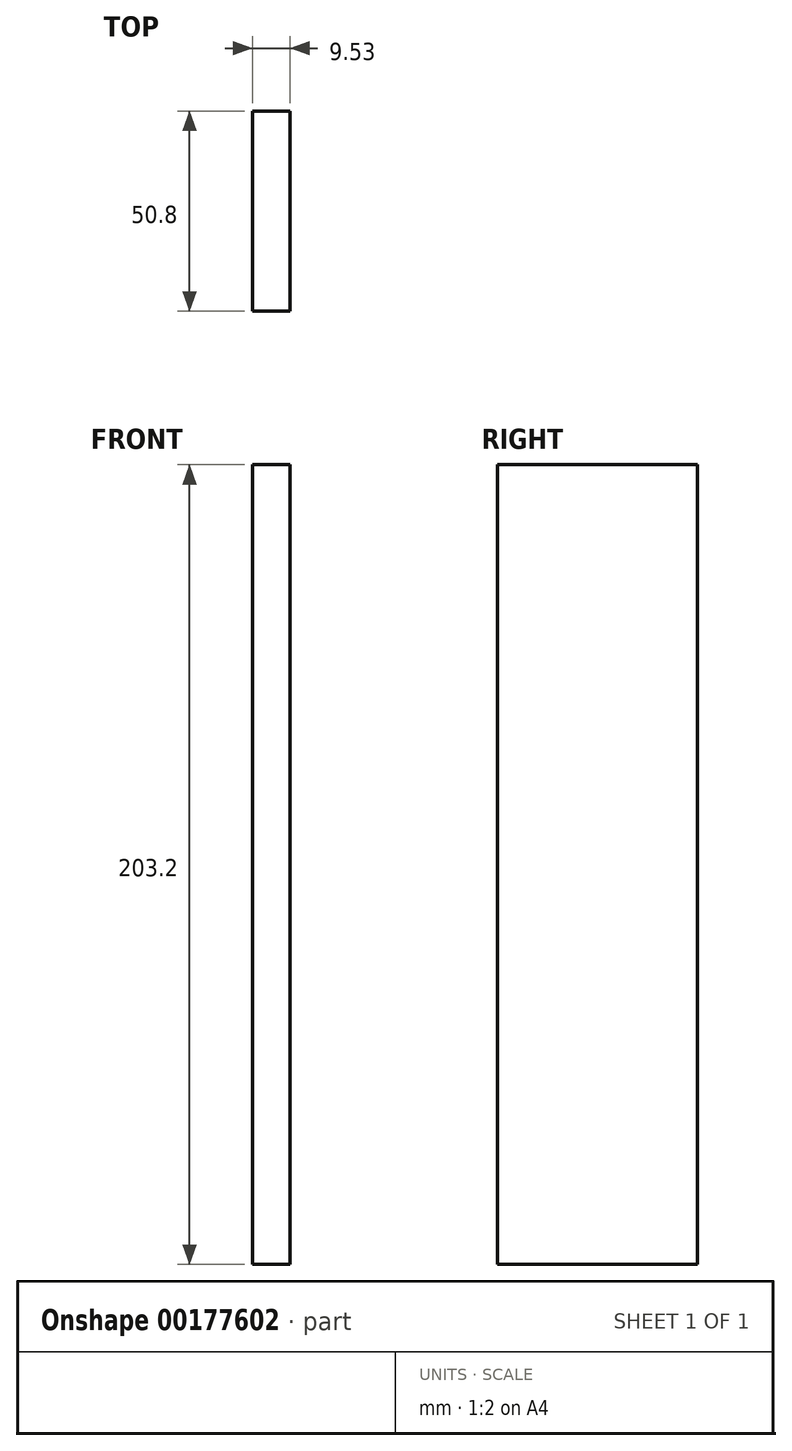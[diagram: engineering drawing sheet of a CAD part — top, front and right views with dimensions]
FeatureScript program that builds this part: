
annotation { "Feature Type Name" : "Feature", "Feature Type Description" : "" }
export const myFeature = defineFeature(function(context is Context, id is Id, definition is map)
    precondition{}
    {
        {
            var Q0;
            Q0=qCreatedBy(makeId("Front.planeOp"),FACE);
            var sketch = newSketch(context, id + "F0", { "sketchPlane" : qUnion([Q0])});
            skLineSegment(sketch, "E0.bottom", {"start": v(-3.84, 157.87) * mm, "end": v(5.69, 157.87) * mm});
            skLineSegment(sketch, "E0.top", {"start": v(-3.84, -45.33) * mm, "end": v(5.69, -45.33) * mm});
            skLineSegment(sketch, "E0.left", {"start": v(-3.84, 157.87) * mm, "end": v(-3.84, -45.33) * mm});
            skLineSegment(sketch, "E0.right", {"start": v(5.69, 157.87) * mm, "end": v(5.69, -45.33) * mm});
            skSolve(sketch);
        }
        {
            var Q0;
            Q0 = qSketchRegion(id + "F0", true);
            extrude(context, id + "F1", {"entities" : qUnion([Q0]), "depth" : 50.8 * mm});
        }
    });
